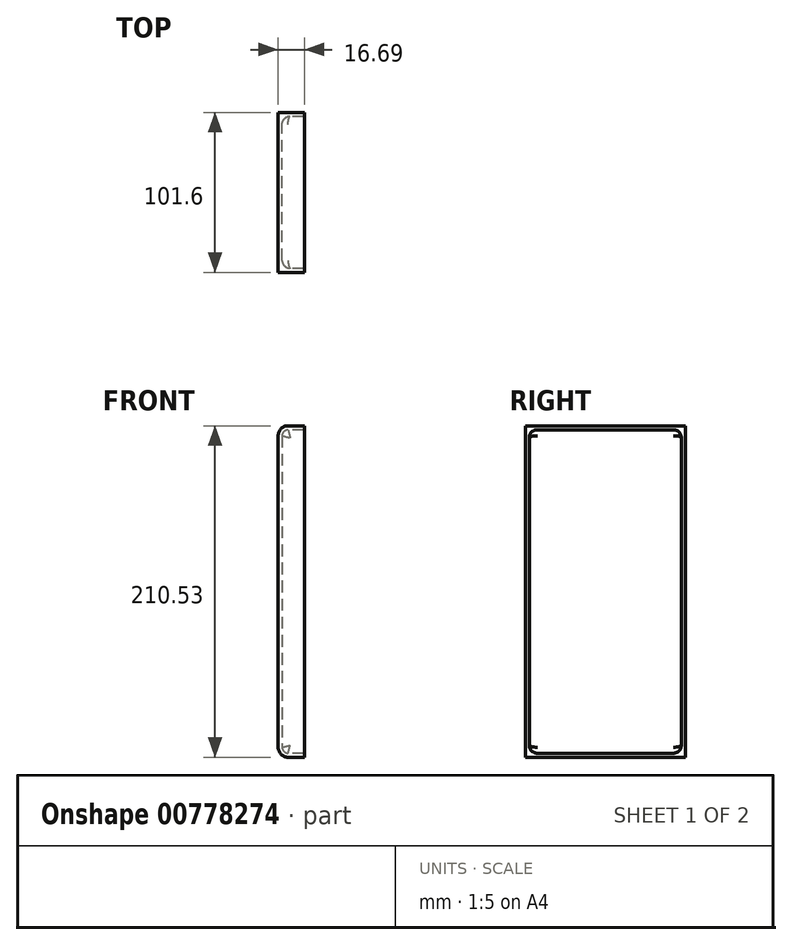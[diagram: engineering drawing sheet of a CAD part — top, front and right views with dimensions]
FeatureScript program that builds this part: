
annotation { "Feature Type Name" : "Feature", "Feature Type Description" : "" }
export const myFeature = defineFeature(function(context is Context, id is Id, definition is map)
    precondition{}
    {
        {
            var Q0;
            Q0=qCreatedBy(makeId("Front.planeOp"),FACE);
            var sketch = newSketch(context, id + "F0", { "sketchPlane" : qUnion([Q0])});
            skLineSegment(sketch, "E0.bottom", {"start": v(0, 104.31) * mm, "end": v(-10.34, 104.31) * mm});
            skLineSegment(sketch, "E0.top", {"start": v(0, -106.22) * mm, "end": v(-10.34, -106.22) * mm});
            skLineSegment(sketch, "E0.left", {"start": v(0, 104.31) * mm, "end": v(0, -106.22) * mm});
            skLineSegment(sketch, "E0.right", {"start": v(-16.69, 97.96) * mm, "end": v(-16.69, -99.87) * mm});
            skPoint(sketch, "E1.visualSharp", {"position": v(-16.69, 104.31) * mm});
            skArc(sketch, "E1.filletArc", {"start": v(-10.34, 104.31) * mm, "mid": v(-14.83, 102.45) * mm, "end": v(-16.69, 97.96) * mm});
            skPoint(sketch, "E2.visualSharp", {"position": v(-16.69, -106.22) * mm});
            skArc(sketch, "E2.filletArc", {"start": v(-16.69, -99.87) * mm, "mid": v(-14.83, -104.36) * mm, "end": v(-10.34, -106.22) * mm});
            skSolve(sketch);
        }
        {
            var Q0;
            Q0=makeQuery(id+"F0.imprint","IMPRINT",FACE,{"disambiguationData":[TD([[makeQuery(id+"F0.imprint","IMPRINT",EDGE,{"derivedFrom":sQuery(id+"F0.wireOp",EDGE,"E0.bottom")}),1.0]])]});
            extrude(context, id + "F1", {"entities" : qUnion([Q0]), "depth" : 101.6 * mm, "offsetDistance" : 25.4 * mm});
        }
        {
            var Q0;
            Q0=makeQuery(id+"F1.opExtrude","SWEPT_FACE",FACE,{"disambiguationData":[OSD([sQuery(id+"F0.wireOp",EDGE,"E0.left")])]});
            shell(context, id + "F2", {"entities" : qUnion([Q0]), "thickness" : 2.54 * mm});
        }
        {
            var Q0;
            Q0=makeQuery(id+"F2.opShell","OFFSET_FACE",FACE,{"disambiguationData":[OSD([sQuery(id+"F0.wireOp",EDGE,"E0.right")])]});
            fillet(context, id + "F3", {"entities" : qUnion([Q0]), "radius" : 5.08 * mm, "tangentPropagation" : true, "allowEdgeOverflow" : false});
        }
    });
